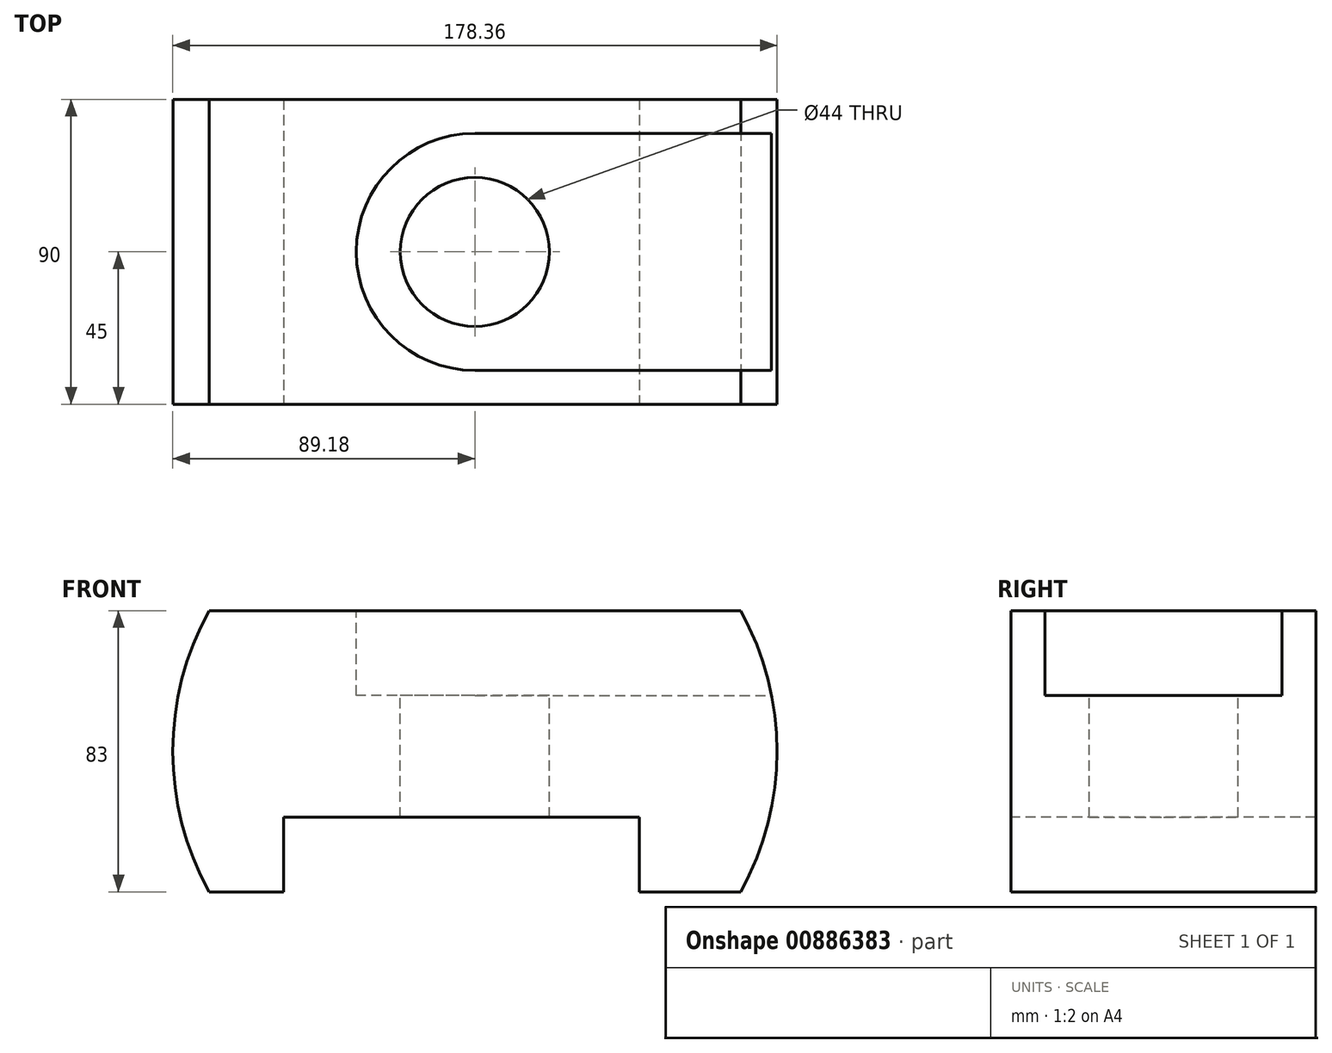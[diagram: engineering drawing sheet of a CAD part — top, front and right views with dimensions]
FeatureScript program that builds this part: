
annotation { "Feature Type Name" : "Feature", "Feature Type Description" : "" }
export const myFeature = defineFeature(function(context is Context, id is Id, definition is map)
    precondition{}
    {
        {
            var Q0;
            Q0=qCreatedBy(makeId("Top.planeOp"),FACE);
            var sketch = newSketch(context, id + "F0", { "sketchPlane" : qUnion([Q0])});
            skLineSegment(sketch, "E0.bottom", {"start": v(78.5, 45) * mm, "end": v(-78.5, 45) * mm});
            skLineSegment(sketch, "E0.top", {"start": v(78.5, -45) * mm, "end": v(-78.5, -45) * mm});
            skLineSegment(sketch, "E0.left", {"start": v(78.5, 45) * mm, "end": v(78.5, -45) * mm});
            skLineSegment(sketch, "E0.right", {"start": v(-78.5, 45) * mm, "end": v(-78.5, -45) * mm});
            skPoint(sketch, "E0.middle", {"position": v(0, 0) * mm});
            skSolve(sketch);
        }
        {
            var Q0;
            Q0 = qSketchRegion(id + "F0", true);
            extrude(context, id + "F1", {"entities" : qUnion([Q0]), "depth" : 83 * mm, "offsetDistance" : 25 * mm});
        }
        {
            var Q0;
            Q0=makeQuery(id+"F1.opExtrude","SWEPT_FACE",FACE,{"disambiguationData":[OSD([sQuery(id+"F0.wireOp",EDGE,"E0.top")])]});
            var sketch = newSketch(context, id + "F2", { "sketchPlane" : qUnion([Q0])});
            skArc(sketch, "E1", {"start": v(-78.5, 83) * mm, "mid": v(-89.18, 41.5) * mm, "end": v(-78.5, 0) * mm});
            skArc(sketch, "E2", {"start": v(78.5, 0) * mm, "mid": v(89.18, 41.5) * mm, "end": v(78.5, 83) * mm});
            skSolve(sketch);
        }
        {
            var Q0;
            Q0=makeQuery(id+"F2.imprint","IMPRINT",FACE,{"disambiguationData":[TD([[makeQuery(id+"F2.imprint","IMPRINT",EDGE,{"derivedFrom":sQuery(id+"F2.wireOp",EDGE,"E1")}),1.0]])]});
            var Q1;
            Q1=makeQuery(id+"F2.imprint","IMPRINT",FACE,{"disambiguationData":[TD([[makeQuery(id+"F2.imprint","IMPRINT",EDGE,{"derivedFrom":sQuery(id+"F2.wireOp",EDGE,"E2")}),1.0]])]});
            var Q2;
            Q2=makeQuery(id+"F1.opExtrude","SWEPT_FACE",FACE,{"disambiguationData":[OSD([sQuery(id+"F0.wireOp",EDGE,"E0.bottom")])]});
            extrude(context, id + "F3", {"entities" : qUnion([Q0, Q1]), "operationType" : NewBodyOperationType.ADD, "endBound" : BoundingType.UP_TO_SURFACE, "oppositeDirection" : true, "depth" : 25 * mm, "endBoundEntityFace" : qUnion([Q2]), "offsetDistance" : 25 * mm});
        }
        {
            var Q0;
            {var subQ0=sQuery(id+"F0.wireOp",EDGE,"E0.top");Q0=makeQuery(id+"F3.boolean.opBoolean","MERGE",FACE,{"derivedFrom":[makeQuery(id+"F1.opExtrude","SWEPT_FACE",FACE,{"disambiguationData":[OSD([subQ0])]}),makeQuery(id+"F3.opExtrude","CAP_FACE",FACE,{"disambiguationData":[OSD([subQ0,sQuery(id+"F0.wireOp",EDGE,"E0.right"),sQuery(id+"F2.wireOp",EDGE,"E1")])],"isStart":true}),makeQuery(id+"F3.opExtrude","CAP_FACE",FACE,{"disambiguationData":[OSD([subQ0,sQuery(id+"F0.wireOp",EDGE,"E0.left"),sQuery(id+"F2.wireOp",EDGE,"E2")])],"isStart":true})]});}
            var sketch = newSketch(context, id + "F4", { "sketchPlane" : qUnion([Q0])});
            skLineSegment(sketch, "E3", {"start": v(-4, 0) * mm, "end": v(-56.5, 0) * mm});
            skLineSegment(sketch, "E4", {"start": v(-56.5, 0) * mm, "end": v(48.5, 0) * mm});
            skLineSegment(sketch, "E5", {"start": v(48.5, 0) * mm, "end": v(48.5, 22) * mm});
            skLineSegment(sketch, "E6", {"start": v(48.5, 22) * mm, "end": v(-56.5, 22) * mm});
            skLineSegment(sketch, "E7", {"start": v(-56.5, 22) * mm, "end": v(-56.5, 0) * mm});
            skSolve(sketch);
        }
        {
            var Q0;
            {var subQ0=sQuery(id+"F4.wireOp",EDGE,"E5");Q0=makeQuery(id+"F4.imprint","IMPRINT",FACE,{"disambiguationData":[TD([[makeQuery(id+"F4.imprint","IMPRINT",EDGE,{"derivedFrom":subQ0}),1.0]])]});}
            extrude(context, id + "F5", {"entities" : qUnion([Q0]), "operationType" : NewBodyOperationType.REMOVE, "oppositeDirection" : true, "depth" : 557 * mm, "offsetDistance" : 25 * mm});
        }
        {
            var Q0;
            Q0=makeQuery(id+"F1.opExtrude","CAP_FACE",FACE,{"disambiguationData":[OSD([sQuery(id+"F0.wireOp",EDGE,"E0.bottom"),sQuery(id+"F0.wireOp",EDGE,"E0.top"),sQuery(id+"F0.wireOp",EDGE,"E0.left"),sQuery(id+"F0.wireOp",EDGE,"E0.right")])],"isStart":false});
            var sketch = newSketch(context, id + "F6", { "sketchPlane" : qUnion([Q0])});
            skCircle(sketch, "E8", {"center": v(0, 0) * mm, "radius": 22 * mm});
            skCircle(sketch, "E9", {"center": v(0, 0) * mm, "radius": 35 * mm});
            skLineSegment(sketch, "E10", {"start": v(0, 35) * mm, "end": v(78.5, 35) * mm});
            skLineSegment(sketch, "E11", {"start": v(0, -35) * mm, "end": v(92.26, -35) * mm});
            skLineSegment(sketch, "E12", {"start": v(78.5, 45) * mm, "end": v(78.5, -45) * mm});
            skLineSegment(sketch, "E13", {"start": v(78.5, 35) * mm, "end": v(93.38, 35) * mm});
            skLineSegment(sketch, "E14", {"start": v(93.38, 35) * mm, "end": v(93.38, -35.54) * mm});
            skLineSegment(sketch, "E15", {"start": v(93.38, -35.54) * mm, "end": v(92.26, -35) * mm});
            skSolve(sketch);
        }
        {
            var Q0;
            Q0 = qSketchRegion(id + "F6", true);
            extrude(context, id + "F7", {"entities" : qUnion([Q0]), "operationType" : NewBodyOperationType.REMOVE, "oppositeDirection" : true, "depth" : 25 * mm, "offsetDistance" : 25 * mm});
        }
        {
            var Q0;
            Q0=makeQuery(id+"F7.boolean.opBoolean","SPLIT",FACE,{"disambiguationData":[TD([makeQuery(id+"F7.opExtrude","SWEPT_FACE",FACE,{"disambiguationData":[OSD([sQuery(id+"F6.wireOp",EDGE,"E8")])]})])],"derivedFrom":makeQuery(id+"F1.opExtrude","CAP_FACE",FACE,{"disambiguationData":[OSD([sQuery(id+"F0.wireOp",EDGE,"E0.bottom"),sQuery(id+"F0.wireOp",EDGE,"E0.top"),sQuery(id+"F0.wireOp",EDGE,"E0.left"),sQuery(id+"F0.wireOp",EDGE,"E0.right")])],"isStart":false})});
            extrude(context, id + "F8", {"entities" : qUnion([Q0]), "operationType" : NewBodyOperationType.REMOVE, "oppositeDirection" : true, "depth" : 185 * mm, "offsetDistance" : 25 * mm});
        }
    });
